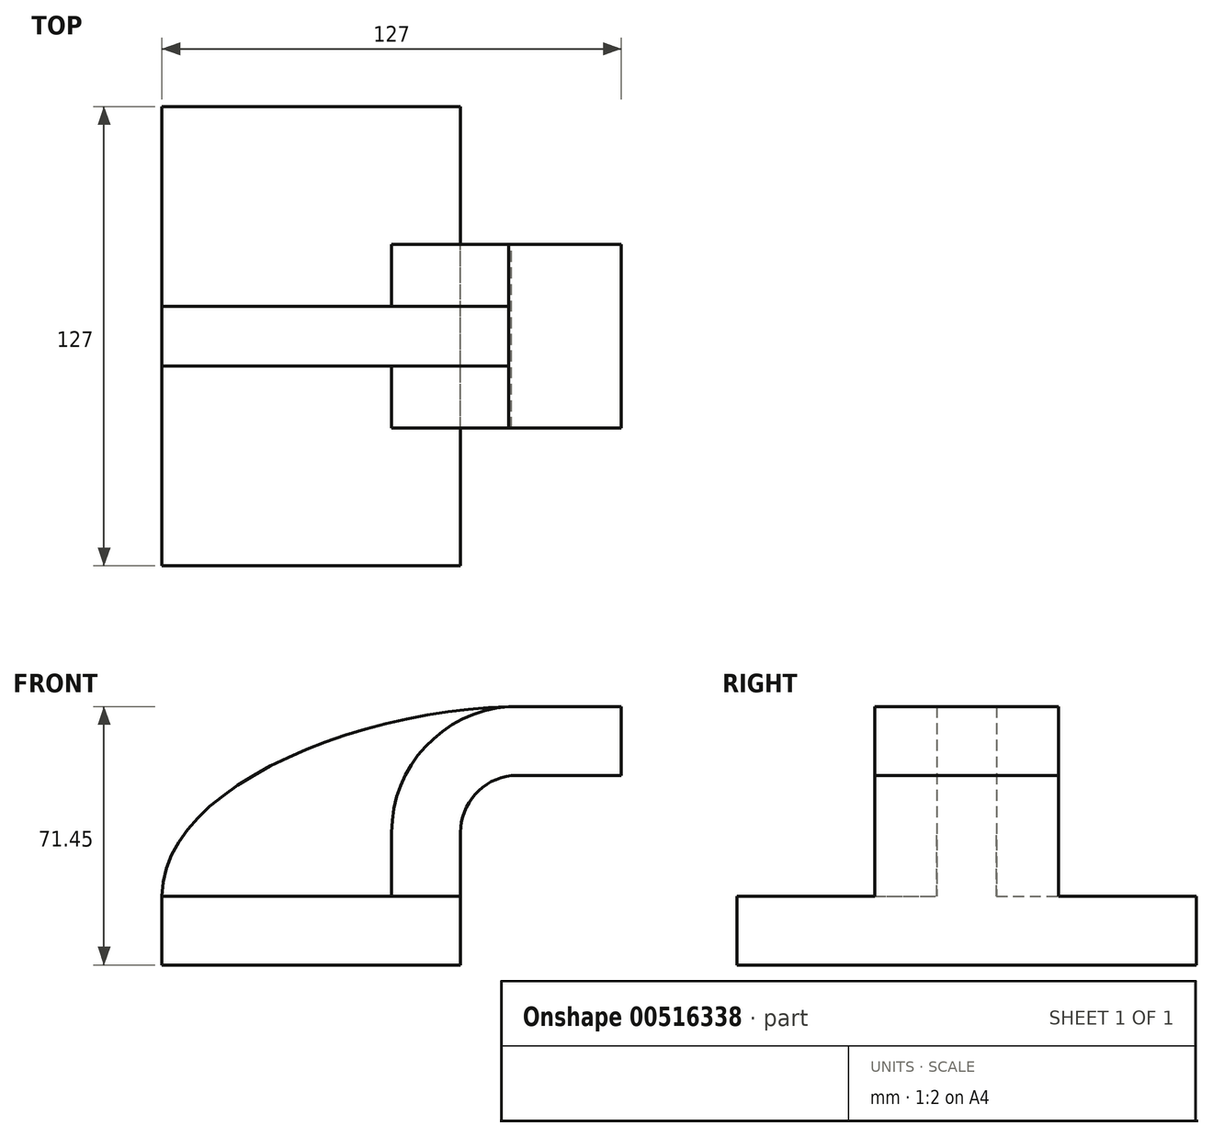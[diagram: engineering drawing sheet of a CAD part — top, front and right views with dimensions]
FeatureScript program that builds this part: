
annotation { "Feature Type Name" : "Feature", "Feature Type Description" : "" }
export const myFeature = defineFeature(function(context is Context, id is Id, definition is map)
    precondition{}
    {
        {
            var Q0;
            Q0=qCreatedBy(makeId("Front.planeOp"),FACE);
            var sketch = newSketch(context, id + "F0", { "sketchPlane" : qUnion([Q0])});
            skLineSegment(sketch, "E0.bottom", {"start": v(-37.17, 11.43) * mm, "end": v(45.38, 11.43) * mm});
            skLineSegment(sketch, "E0.top", {"start": v(-37.17, -7.62) * mm, "end": v(45.38, -7.62) * mm});
            skLineSegment(sketch, "E0.left", {"start": v(-37.17, 11.43) * mm, "end": v(-37.17, -7.62) * mm});
            skLineSegment(sketch, "E0.right", {"start": v(45.38, 11.43) * mm, "end": v(45.38, -7.62) * mm});
            skLineSegment(sketch, "E1.bottom", {"start": v(66.46, 68.58) * mm, "end": v(117.26, 68.58) * mm});
            skLineSegment(sketch, "E1.top", {"start": v(66.46, 40) * mm, "end": v(117.26, 40) * mm});
            skLineSegment(sketch, "E1.left", {"start": v(66.46, 68.58) * mm, "end": v(66.46, 40) * mm});
            skLineSegment(sketch, "E1.right", {"start": v(117.26, 68.58) * mm, "end": v(117.26, 40) * mm});
            skLineSegment(sketch, "E2", {"start": v(45.38, 11.43) * mm, "end": v(45.38, 29) * mm});
            skArc(sketch, "E3", {"start": v(59.49, 44.78) * mm, "mid": v(49.42, 39.58) * mm, "end": v(45.38, 29) * mm});
            skLineSegment(sketch, "E4", {"start": v(59.49, 44.78) * mm, "end": v(89.83, 44.78) * mm});
            skArc(sketch, "E5.1", {"start": v(58.63, 63.83) * mm, "mid": v(35.65, 52.75) * mm, "end": v(26.33, 29) * mm});
            skLineSegment(sketch, "E5.2", {"start": v(26.33, 11.3) * mm, "end": v(26.33, 29) * mm});
            skLineSegment(sketch, "E6", {"start": v(89.83, 68.58) * mm, "end": v(89.83, 40) * mm});
            skPoint(sketch, "E6.endSnap0", {"position": v(91.86, 40) * mm});
            skFitSpline(sketch, "E7", {"points": [v(58.63, 63.83) * mm, v(-37.17, 11.43) * mm], "startDerivative": vector(-124.69, -3.02) * mm, "endDerivative": vector(-0.34, -90.9) * mm});
            skLineSegment(sketch, "E8", {"start": v(58.63, 63.83) * mm, "end": v(89.83, 63.83) * mm});
            skSolve(sketch);
        }
        {
            var Q0;
            Q0=makeQuery(id+"F0.imprint","IMPRINT",FACE,{"disambiguationData":[TD([[makeQuery(id+"F0.imprint","IMPRINT",EDGE,{"derivedFrom":sQuery(id+"F0.wireOp",EDGE,"E0.top")}),1.0]])]});
            extrude(context, id + "F1", {"entities" : qUnion([Q0]), "endBound" : BoundingType.SYMMETRIC, "depth" : 127 * mm, "offsetDistance" : 25.4 * mm});
        }
        {
            var Q0;
            {var subQ4=sQuery(id+"F0.wireOp",EDGE,"E5.1");Q0=makeQuery(id+"F0.imprint","IMPRINT",FACE,{"disambiguationData":[TD([[makeQuery(id+"F0.imprint","IMPRINT",EDGE,{"derivedFrom":subQ4}),-1.0]])]});}
            extrude(context, id + "F2", {"entities" : qUnion([Q0]), "operationType" : NewBodyOperationType.ADD, "endBound" : BoundingType.SYMMETRIC, "depth" : 16.5 * mm, "offsetDistance" : 25.4 * mm});
        }
        {
            var Q0;
            {var subQ1=sQuery(id+"F0.wireOp",EDGE,"E2");Q0=makeQuery(id+"F0.imprint","IMPRINT",FACE,{"disambiguationData":[TD([[makeQuery(id+"F0.imprint","IMPRINT",EDGE,{"derivedFrom":subQ1}),1.0]])]});}
            var Q1;
            {var subQ0=sQuery(id+"F0.wireOp",EDGE,"E8");var subQ1=sQuery(id+"F0.wireOp",EDGE,"E1.left");var subQ2=makeQuery(id+"F0.imprint","INTERSECT",VERTEX,{"derivedFrom":[subQ1,subQ0]});Q1=makeQuery(id+"F0.imprint","IMPRINT",FACE,{"disambiguationData":[TD([[makeQuery(id+"F0.imprint","IMPRINT",EDGE,{"disambiguationData":[TD([[subQ2,-1.0]])],"derivedFrom":subQ1}),1.0]])]});}
            extrude(context, id + "F3", {"entities" : qUnion([Q0, Q1]), "operationType" : NewBodyOperationType.ADD, "endBound" : BoundingType.SYMMETRIC, "depth" : 50.8 * mm, "offsetDistance" : 25.4 * mm});
        }
    });
